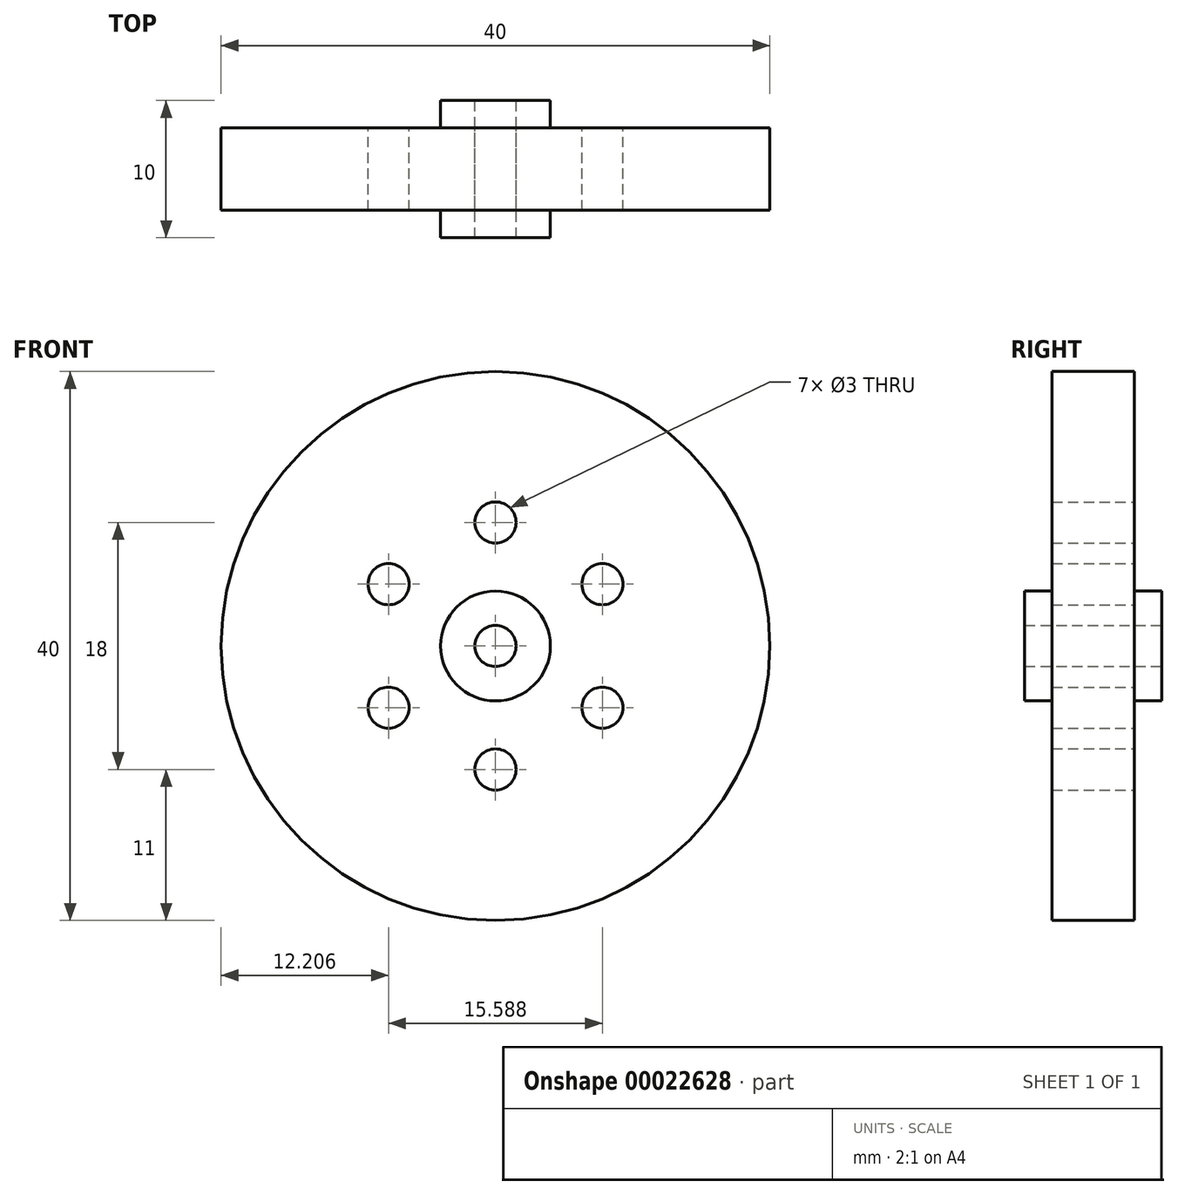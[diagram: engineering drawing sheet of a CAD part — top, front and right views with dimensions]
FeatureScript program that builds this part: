
annotation { "Feature Type Name" : "Feature", "Feature Type Description" : "" }
export const myFeature = defineFeature(function(context is Context, id is Id, definition is map)
    precondition{}
    {
        {
            var Q0;
            Q0=qCreatedBy(makeId("Front.planeOp"),FACE);
            var sketch = newSketch(context, id + "F0", { "sketchPlane" : qUnion([Q0])});
            skCircle(sketch, "E0", {"center": v(0, 0) * mm, "radius": 20 * mm});
            skCircle(sketch, "E1", {"center": v(0, 9) * mm, "radius": 1.5 * mm});
            skCircle(sketch, "E2", {"center": v(0, 0) * mm, "radius": 1.5 * mm});
            skCircle(sketch, "E3.1.0", {"center": v(-7.8, 4.5) * mm, "radius": 1.5 * mm});
            skCircle(sketch, "E3.2.0", {"center": v(-7.8, -4.5) * mm, "radius": 1.5 * mm});
            skCircle(sketch, "E3.3.0", {"center": v(0, -9) * mm, "radius": 1.5 * mm});
            skCircle(sketch, "E3.4.0", {"center": v(7.8, -4.5) * mm, "radius": 1.5 * mm});
            skCircle(sketch, "E3.5.0", {"center": v(7.8, 4.5) * mm, "radius": 1.5 * mm});
            skSolve(sketch);
        }
        {
            var Q0;
            Q0=makeQuery(id+"F0.imprint","IMPRINT",FACE,{"disambiguationData":[TD([[makeQuery(id+"F0.imprint","IMPRINT",EDGE,{"derivedFrom":sQuery(id+"F0.wireOp",EDGE,"E0")}),1.0]])]});
            extrude(context, id + "F1", {"entities" : qUnion([Q0]), "depth" : 6 * mm});
        }
        {
            var Q0;
            Q0=makeQuery(id+"F1.opExtrude","CAP_FACE",FACE,{"disambiguationData":[OSD([sQuery(id+"F0.wireOp",EDGE,"E0"),sQuery(id+"F0.wireOp",EDGE,"E1"),sQuery(id+"F0.wireOp",EDGE,"E2"),sQuery(id+"F0.wireOp",EDGE,"E3.1.0"),sQuery(id+"F0.wireOp",EDGE,"E3.2.0"),sQuery(id+"F0.wireOp",EDGE,"E3.3.0"),sQuery(id+"F0.wireOp",EDGE,"E3.4.0"),sQuery(id+"F0.wireOp",EDGE,"E3.5.0")])],"isStart":false});
            var sketch = newSketch(context, id + "F2", { "sketchPlane" : qUnion([Q0])});
            skCircle(sketch, "E4", {"center": v(0, 0) * mm, "radius": 4 * mm});
            skSolve(sketch);
        }
        {
            var Q0;
            Q0 = qSketchRegion(id + "F2", true);
            extrude(context, id + "F3", {"entities" : qUnion([Q0]), "operationType" : NewBodyOperationType.ADD, "depth" : 2 * mm});
        }
        {
            var Q0;
            Q0 = qSketchRegion(id + "F2", true);
            extrude(context, id + "F4", {"entities" : qUnion([Q0]), "operationType" : NewBodyOperationType.ADD, "oppositeDirection" : true, "depth" : 8 * mm});
        }
        {
            var Q0;
            Q0=makeQuery(id+"F4.opExtrude","CAP_FACE",FACE,{"disambiguationData":[OSD([sQuery(id+"F2.wireOp",EDGE,"E4")])],"isStart":false});
            var sketch = newSketch(context, id + "F5", { "sketchPlane" : qUnion([Q0])});
            skCircle(sketch, "E5", {"center": v(0, 0) * mm, "radius": 1.5 * mm});
            skSolve(sketch);
        }
        {
            var Q0;
            Q0 = qSketchRegion(id + "F5", true);
            extrude(context, id + "F6", {"entities" : qUnion([Q0]), "operationType" : NewBodyOperationType.REMOVE, "oppositeDirection" : true, "depth" : 127 * mm});
        }
    });
